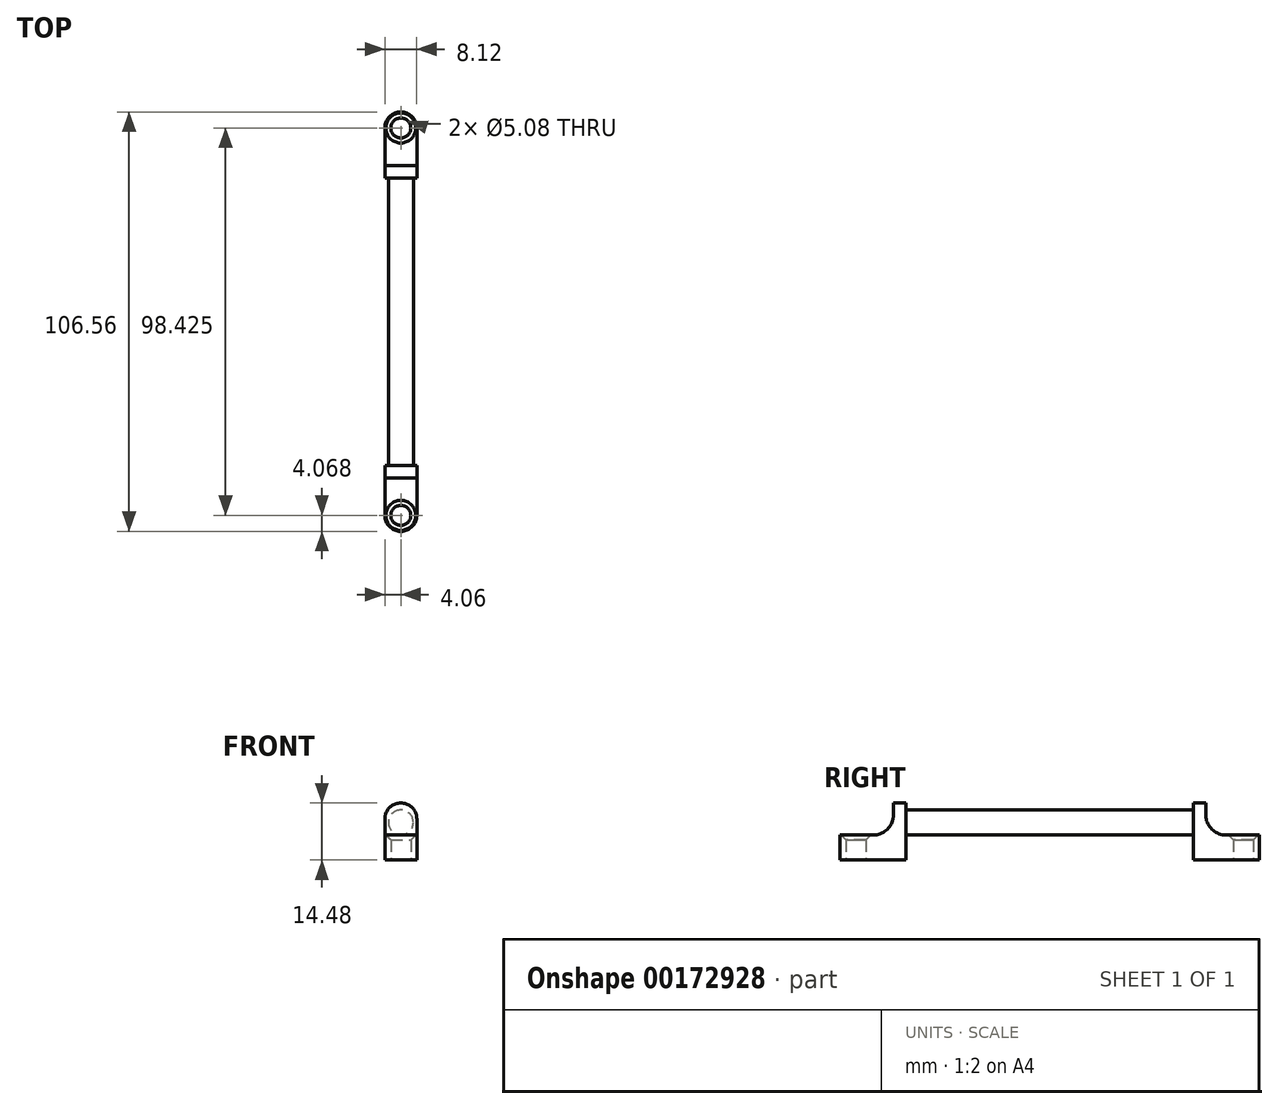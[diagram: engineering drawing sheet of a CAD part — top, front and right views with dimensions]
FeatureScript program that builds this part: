
annotation { "Feature Type Name" : "Feature", "Feature Type Description" : "" }
export const myFeature = defineFeature(function(context is Context, id is Id, definition is map)
    precondition{}
    {
        {
            var Q0;
            Q0=qCreatedBy(makeId("Front.planeOp"),FACE);
            var sketch = newSketch(context, id + "F0", { "sketchPlane" : qUnion([Q0])});
            skArc(sketch, "E0", {"start": v(4.06, 10.41) * mm, "mid": v(0, 14.48) * mm, "end": v(-4.06, 10.41) * mm});
            skCircle(sketch, "E1", {"center": v(0, 9.53) * mm, "radius": 3.18 * mm});
            skLineSegment(sketch, "E2", {"start": v(0, 10.41) * mm, "end": v(-4.06, 10.41) * mm, "construction": true});
            skLineSegment(sketch, "E3", {"start": v(-4.06, 10.41) * mm, "end": v(-4.06, 0) * mm});
            skLineSegment(sketch, "E4", {"start": v(-4.06, 0) * mm, "end": v(4.06, 0) * mm});
            skLineSegment(sketch, "E5", {"start": v(4.06, 0) * mm, "end": v(4.06, 10.41) * mm});
            skLineSegment(sketch, "E6", {"start": v(4.06, 10.41) * mm, "end": v(0, 10.41) * mm, "construction": true});
            skSolve(sketch);
        }
        {
            var Q0;
            Q0 = qSketchRegion(id + "F0", true);
            extrude(context, id + "F1", {"entities" : qUnion([Q0]), "endBound" : BoundingType.SYMMETRIC, "depth" : 79.38 * mm});
        }
        {
            var Q0;
            Q0=qCreatedBy(makeId("Right.planeOp"),FACE);
            var sketch = newSketch(context, id + "F2", { "sketchPlane" : qUnion([Q0])});
            skLineSegment(sketch, "E7.bottom", {"start": v(-36.51, 15.23) * mm, "end": v(36.51, 15.23) * mm});
            skLineSegment(sketch, "E7.top", {"start": v(-36.51, -2.95) * mm, "end": v(36.51, -2.95) * mm});
            skLineSegment(sketch, "E7.left", {"start": v(-36.51, 15.23) * mm, "end": v(-36.51, -2.95) * mm});
            skLineSegment(sketch, "E7.right", {"start": v(36.51, 15.23) * mm, "end": v(36.51, -2.95) * mm});
            skPoint(sketch, "E7.middle", {"position": v(0, 6.14) * mm});
            skSolve(sketch);
        }
        {
            var Q0;
            Q0 = qSketchRegion(id + "F2", true);
            extrude(context, id + "F3", {"entities" : qUnion([Q0]), "operationType" : NewBodyOperationType.REMOVE, "endBound" : BoundingType.SYMMETRIC, "oppositeDirection" : true, "depth" : 25.4 * mm});
        }
        {
            var Q0;
            Q0=makeQuery(id+"F1.opExtrude","CAP_FACE",FACE,{"disambiguationData":[OSD([sQuery(id+"F0.wireOp",EDGE,"E0"),sQuery(id+"F0.wireOp",EDGE,"E1"),sQuery(id+"F0.wireOp",EDGE,"E3"),sQuery(id+"F0.wireOp",EDGE,"E4"),sQuery(id+"F0.wireOp",EDGE,"E5")])],"isStart":false});
            var sketch = newSketch(context, id + "F4", { "sketchPlane" : qUnion([Q0])});
            skCircle(sketch, "E8.0", {"center": v(0, 9.53) * mm, "radius": 3.18 * mm});
            skSolve(sketch);
        }
        {
            var Q0;
            Q0 = qSketchRegion(id + "F4", true);
            extrude(context, id + "F5", {"entities" : qUnion([Q0]), "operationType" : NewBodyOperationType.ADD, "oppositeDirection" : true, "depth" : 79.38 * mm});
        }
        {
            var Q0;
            Q0=qCreatedBy(makeId("Right.planeOp"),FACE);
            var sketch = newSketch(context, id + "F6", { "sketchPlane" : qUnion([Q0])});
            skLineSegment(sketch, "E9.bottom", {"start": v(-26.04, 4.44) * mm, "end": v(-35.56, 4.44) * mm});
            skLineSegment(sketch, "E9.top", {"start": v(-26.04, 1.27) * mm, "end": v(-35.56, 1.27) * mm});
            skLineSegment(sketch, "E9.left", {"start": v(-26.04, 4.45) * mm, "end": v(-26.04, 1.27) * mm});
            skLineSegment(sketch, "E9.right", {"start": v(-35.56, 4.44) * mm, "end": v(-35.56, 1.27) * mm});
            skPoint(sketch, "E9.middle", {"position": v(-30.8, 2.86) * mm});
            skLineSegment(sketch, "E10.bottom", {"start": v(35.56, 4.45) * mm, "end": v(26.04, 4.45) * mm});
            skLineSegment(sketch, "E10.top", {"start": v(35.56, 1.27) * mm, "end": v(26.04, 1.27) * mm});
            skLineSegment(sketch, "E10.left", {"start": v(35.56, 4.45) * mm, "end": v(35.56, 1.27) * mm});
            skLineSegment(sketch, "E10.right", {"start": v(26.04, 4.45) * mm, "end": v(26.04, 1.27) * mm});
            skPoint(sketch, "E10.middle", {"position": v(30.8, 2.86) * mm});
            skLineSegment(sketch, "E11", {"start": v(-30.8, 2.86) * mm, "end": v(0, 0) * mm, "construction": true});
            skLineSegment(sketch, "E12", {"start": v(0, 0) * mm, "end": v(30.8, 2.86) * mm, "construction": true});
            skLineSegment(sketch, "E13", {"start": v(-30.8, 2.86) * mm, "end": v(30.8, 2.86) * mm, "construction": true});
            skSolve(sketch);
        }
        {
            var Q0;
            Q0 = qSketchRegion(id + "F6", true);
            extrude(context, id + "F7", {"entities" : qUnion([Q0]), "operationType" : NewBodyOperationType.REMOVE, "endBound" : BoundingType.SYMMETRIC, "oppositeDirection" : true, "depth" : 25.4 * mm});
        }
        {
            var Q0;
            {var subQ1=sQuery(id+"F0.wireOp",EDGE,"E4");Q0=makeQuery(id+"F3.boolean.opBoolean","SPLIT",FACE,{"disambiguationData":[TD([makeQuery(id+"F3.opExtrude","SWEPT_FACE",FACE,{"disambiguationData":[OSD([sQuery(id+"F2.wireOp",EDGE,"E7.left")])]})])],"derivedFrom":makeQuery(id+"F1.opExtrude","SWEPT_FACE",FACE,{"disambiguationData":[OSD([subQ1])]})});}
            var sketch = newSketch(context, id + "F8", { "sketchPlane" : qUnion([Q0])});
            skLineSegment(sketch, "E14", {"start": v(4.06, 36.51) * mm, "end": v(-4.06, 36.51) * mm});
            skLineSegment(sketch, "E15", {"start": v(-4.06, 36.51) * mm, "end": v(-4.06, 49.21) * mm});
            skArc(sketch, "E16", {"start": v(4.06, 49.21) * mm, "mid": v(0, 53.28) * mm, "end": v(-4.06, 49.21) * mm});
            skLineSegment(sketch, "E17", {"start": v(4.06, 49.21) * mm, "end": v(4.06, 36.51) * mm});
            skLineSegment(sketch, "E18", {"start": v(-4.06, 49.21) * mm, "end": v(4.06, 49.21) * mm, "construction": true});
            skCircle(sketch, "E19", {"center": v(0, 49.21) * mm, "radius": 2.54 * mm});
            skLineSegment(sketch, "E20.MirrorCS", {"start": v(-4.06, -49.21) * mm, "end": v(4.06, -49.21) * mm, "construction": true});
            skLineSegment(sketch, "E21.MirrorCS", {"start": v(4.06, -49.21) * mm, "end": v(4.06, -36.51) * mm});
            skLineSegment(sketch, "E22.MirrorCS", {"start": v(4.06, -36.51) * mm, "end": v(-4.06, -36.51) * mm});
            skArc(sketch, "E23.MirrorCS", {"start": v(4.06, -49.21) * mm, "mid": v(0, -53.28) * mm, "end": v(-4.06, -49.21) * mm});
            skLineSegment(sketch, "E24.MirrorCS", {"start": v(-4.06, -36.51) * mm, "end": v(-4.06, -49.21) * mm});
            skCircle(sketch, "E25.MirrorC", {"center": v(0, -49.21) * mm, "radius": 2.54 * mm});
            skSolve(sketch);
        }
        {
            var Q0;
            Q0 = qSketchRegion(id + "F8", true);
            extrude(context, id + "F9", {"entities" : qUnion([Q0]), "operationType" : NewBodyOperationType.ADD, "oppositeDirection" : true, "depth" : 6.35 * mm});
        }
        {
            var Q0;
            Q0=makeQuery(id+"F9.boolean.opBoolean","INTERSECT",EDGE,{"derivedFrom":[makeQuery(id+"F5.boolean.opBoolean","MERGE",FACE,{"derivedFrom":[makeQuery(id+"F1.opExtrude","CAP_FACE",FACE,{"disambiguationData":[OSD([sQuery(id+"F0.wireOp",EDGE,"E0"),sQuery(id+"F0.wireOp",EDGE,"E1"),sQuery(id+"F0.wireOp",EDGE,"E3"),sQuery(id+"F0.wireOp",EDGE,"E4"),sQuery(id+"F0.wireOp",EDGE,"E5")])],"isStart":true}),makeQuery(id+"F5.opExtrude","CAP_FACE",FACE,{"disambiguationData":[OSD([sQuery(id+"F4.wireOp",EDGE,"E8.0")])],"isStart":false})]}),makeQuery(id+"F9.opExtrude","CAP_FACE",FACE,{"disambiguationData":[OSD([sQuery(id+"F8.wireOp",EDGE,"E21.MirrorCS"),sQuery(id+"F8.wireOp",EDGE,"E22.MirrorCS"),sQuery(id+"F8.wireOp",EDGE,"E23.MirrorCS"),sQuery(id+"F8.wireOp",EDGE,"E24.MirrorCS"),sQuery(id+"F8.wireOp",EDGE,"E25.MirrorC")])],"isStart":false})]});
            var Q1;
            Q1=makeQuery(id+"F9.boolean.opBoolean","INTERSECT",EDGE,{"derivedFrom":[makeQuery(id+"F5.boolean.opBoolean","MERGE",FACE,{"derivedFrom":[makeQuery(id+"F1.opExtrude","CAP_FACE",FACE,{"disambiguationData":[OSD([sQuery(id+"F0.wireOp",EDGE,"E0"),sQuery(id+"F0.wireOp",EDGE,"E1"),sQuery(id+"F0.wireOp",EDGE,"E3"),sQuery(id+"F0.wireOp",EDGE,"E4"),sQuery(id+"F0.wireOp",EDGE,"E5")])],"isStart":false}),makeQuery(id+"F5.opExtrude","CAP_FACE",FACE,{"disambiguationData":[OSD([sQuery(id+"F4.wireOp",EDGE,"E8.0")])],"isStart":true})]}),makeQuery(id+"F9.opExtrude","CAP_FACE",FACE,{"disambiguationData":[OSD([sQuery(id+"F8.wireOp",EDGE,"E14"),sQuery(id+"F8.wireOp",EDGE,"E15"),sQuery(id+"F8.wireOp",EDGE,"E16"),sQuery(id+"F8.wireOp",EDGE,"E17"),sQuery(id+"F8.wireOp",EDGE,"E19")])],"isStart":false})]});
            fillet(context, id + "F10", {"entities" : qUnion([Q0, Q1]), "radius" : 5.08 * mm, "tangentPropagation" : true, "allowEdgeOverflow" : false});
        }
        {
            var Q0;
            Q0=makeQuery(id+"F9.opExtrude","CAP_EDGE",EDGE,{"disambiguationData":[OSD([sQuery(id+"F8.wireOp",EDGE,"E19")])],"isStart":false});
            var Q1;
            Q1=makeQuery(id+"F9.opExtrude","CAP_EDGE",EDGE,{"disambiguationData":[OSD([sQuery(id+"F8.wireOp",EDGE,"E25.MirrorC")])],"isStart":false});
            chamfer(context, id + "F11", {"entities" : qUnion([Q0, Q1]), "width" : 1.27 * mm, "tangentPropagation" : true});
        }
    });
